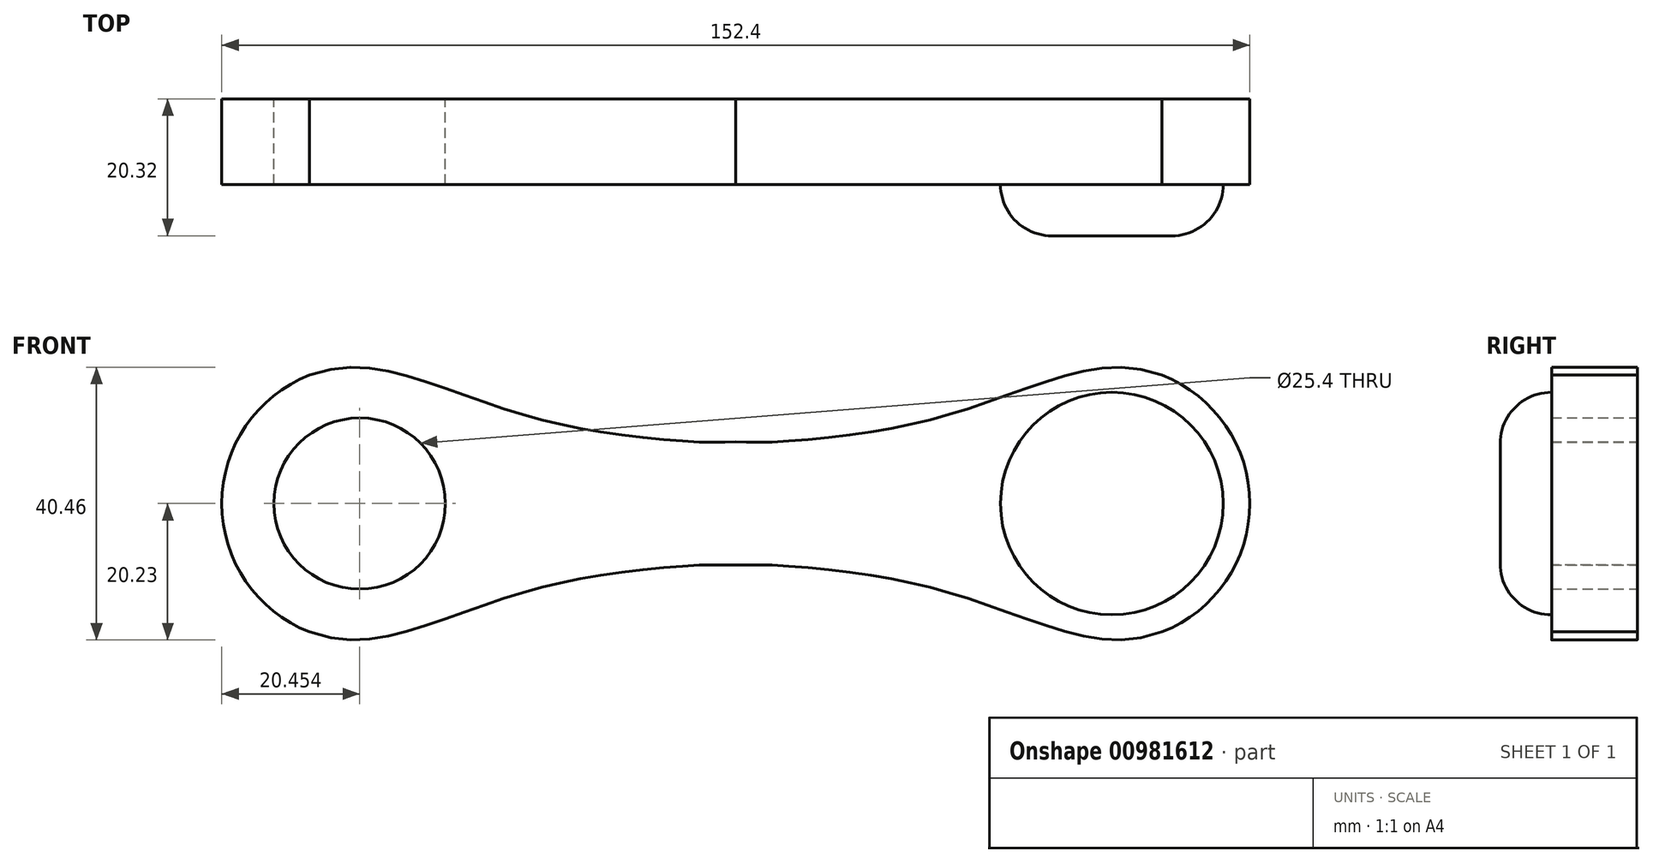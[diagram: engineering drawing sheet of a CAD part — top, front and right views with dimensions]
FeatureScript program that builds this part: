
annotation { "Feature Type Name" : "Feature", "Feature Type Description" : "" }
export const myFeature = defineFeature(function(context is Context, id is Id, definition is map)
    precondition{}
    {
        {
            var Q0;
            Q0=qCreatedBy(makeId("Front.planeOp"),FACE);
            var sketch = newSketch(context, id + "F0", { "sketchPlane" : qUnion([Q0])});
            skArc(sketch, "E0", {"start": v(63.2, -19.05) * mm, "mid": v(76.2, 0) * mm, "end": v(63.2, 19.05) * mm});
            skCircle(sketch, "E1", {"center": v(55.75, 0) * mm, "radius": 16.51 * mm});
            skFitSpline(sketch, "E2", {"points": [v(63.2, 19.05) * mm, v(49.1, 19.05) * mm, v(34.52, 14.12) * mm, v(20.1, 10.64) * mm, v(5.51, 9.15) * mm, v(0, 9.15) * mm], "startDerivative": vector(-75.01, 26.4) * mm, "endDerivative": vector(-36.15, 1.1) * mm});
            skFitSpline(sketch, "E3.MirrorCS", {"points": [v(-63.2, 19.05) * mm, v(-49.1, 19.05) * mm, v(-34.52, 14.12) * mm, v(-20.1, 10.64) * mm, v(-5.51, 9.15) * mm, v(0, 9.15) * mm], "startDerivative": vector(75.01, 26.4) * mm, "endDerivative": vector(36.15, 1.1) * mm});
            skArc(sketch, "E4.MirrorCS", {"start": v(-63.2, -19.05) * mm, "mid": v(-76.2, 0) * mm, "end": v(-63.2, 19.05) * mm});
            skFitSpline(sketch, "E5.MirrorCS", {"points": [v(63.2, -19.05) * mm, v(49.1, -19.05) * mm, v(34.52, -14.12) * mm, v(20.1, -10.64) * mm, v(5.51, -9.15) * mm, v(0, -9.15) * mm], "startDerivative": vector(-75.01, -26.4) * mm, "endDerivative": vector(-36.15, -1.1) * mm});
            skFitSpline(sketch, "E6.MirrorCS", {"points": [v(-63.2, -19.05) * mm, v(-49.1, -19.05) * mm, v(-34.52, -14.12) * mm, v(-20.1, -10.64) * mm, v(-5.51, -9.15) * mm, v(0, -9.15) * mm], "startDerivative": vector(75.01, -26.4) * mm, "endDerivative": vector(36.15, -1.1) * mm});
            skCircle(sketch, "E7", {"center": v(-55.75, 0) * mm, "radius": 12.7 * mm});
            skSolve(sketch);
        }
        {
            var Q0;
            Q0=makeQuery(id+"F0.imprint","IMPRINT",FACE,{"disambiguationData":[TD([[makeQuery(id+"F0.imprint","IMPRINT",EDGE,{"derivedFrom":sQuery(id+"F0.wireOp",EDGE,"E0")}),1.0]])]});
            extrude(context, id + "F1", {"entities" : qUnion([Q0]), "depth" : 12.7 * mm, "offsetDistance" : 25.4 * mm});
        }
        {
            var Q0;
            Q0=makeQuery(id+"F0.imprint","IMPRINT",FACE,{"disambiguationData":[TD([[makeQuery(id+"F0.imprint","IMPRINT",EDGE,{"derivedFrom":sQuery(id+"F0.wireOp",EDGE,"E1")}),1.0]])]});
            extrude(context, id + "F2", {"entities" : qUnion([Q0]), "operationType" : NewBodyOperationType.ADD, "depth" : 20.32 * mm, "offsetDistance" : 25.4 * mm});
        }
        {
            var Q0;
            Q0=makeQuery(id+"F2.opExtrude","CAP_FACE",FACE,{"disambiguationData":[OSD([sQuery(id+"F0.wireOp",EDGE,"E1")])],"isStart":false});
            fillet(context, id + "F3", {"entities" : qUnion([Q0]), "radius" : 7.62 * mm, "tangentPropagation" : true, "allowEdgeOverflow" : false});
        }
    });
